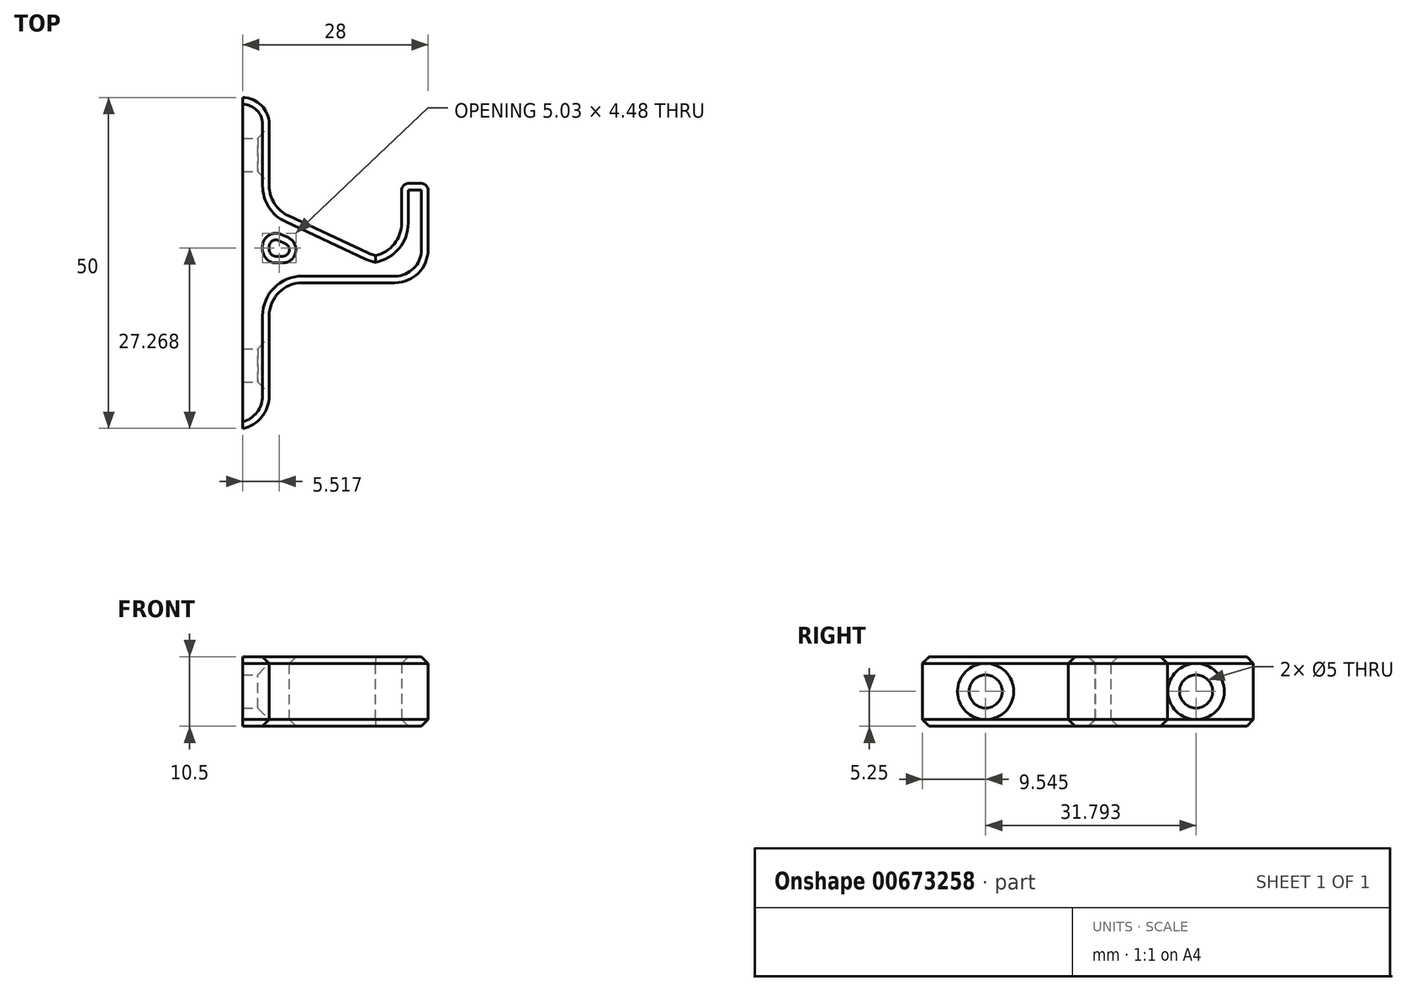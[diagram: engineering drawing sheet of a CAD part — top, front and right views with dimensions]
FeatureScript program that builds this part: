
annotation { "Feature Type Name" : "Feature", "Feature Type Description" : "" }
export const myFeature = defineFeature(function(context is Context, id is Id, definition is map)
    precondition{}
    {
        {
            var Q0;
            Q0=qCreatedBy(makeId("Top.planeOp"),FACE);
            var sketch = newSketch(context, id + "F0", { "sketchPlane" : qUnion([Q0])});
            skLineSegment(sketch, "E0", {"start": v(-37.83, 27.26) * mm, "end": v(-37.83, -22.74) * mm});
            skLineSegment(sketch, "E1", {"start": v(-37.83, -22.74) * mm, "end": v(-33.83, -22.74) * mm});
            skLineSegment(sketch, "E2", {"start": v(-33.83, -22.74) * mm, "end": v(-33.83, -0.71) * mm});
            skLineSegment(sketch, "E3", {"start": v(-33.83, -0.71) * mm, "end": v(-9.83, -0.71) * mm});
            skLineSegment(sketch, "E4", {"start": v(-9.83, -0.71) * mm, "end": v(-9.83, 14.29) * mm});
            skLineSegment(sketch, "E5", {"start": v(-9.83, 14.29) * mm, "end": v(-13.83, 14.29) * mm});
            skLineSegment(sketch, "E6", {"start": v(-13.83, 14.29) * mm, "end": v(-13.83, 3.29) * mm});
            skLineSegment(sketch, "E7", {"start": v(-13.83, 3.29) * mm, "end": v(-33.83, 3.29) * mm});
            skLineSegment(sketch, "E8", {"start": v(-33.83, 3.29) * mm, "end": v(-33.83, 27.26) * mm});
            skLineSegment(sketch, "E9", {"start": v(-33.83, 27.26) * mm, "end": v(-37.83, 27.26) * mm});
            skLineSegment(sketch, "E10", {"start": v(-33.83, 6.34) * mm, "end": v(-27.28, 3.29) * mm});
            skLineSegment(sketch, "E11", {"start": v(-27.28, 3.29) * mm, "end": v(-17.81, 3.29) * mm});
            skLineSegment(sketch, "E12", {"start": v(-17.81, 3.29) * mm, "end": v(-33.83, 10.76) * mm});
            skLineSegment(sketch, "E13", {"start": v(-33.83, -8.74) * mm, "end": v(741.82, -0.71) * mm});
            skLineSegment(sketch, "E14", {"start": v(-33.83, -4.74) * mm, "end": v(355.5, -0.71) * mm});
            skSolve(sketch);
        }
        {
            var Q0;
            Q0=makeQuery(id+"F0.imprint","IMPRINT",FACE,{"disambiguationData":[TD([[makeQuery(id+"F0.imprint","IMPRINT",EDGE,{"derivedFrom":sQuery(id+"F0.wireOp",EDGE,"E0")}),1.0]])]});
            var Q1;
            {var subQ0=sQuery(id+"F0.wireOp",EDGE,"E10");Q1=makeQuery(id+"F0.imprint","IMPRINT",FACE,{"disambiguationData":[TD([[makeQuery(id+"F0.imprint","IMPRINT",EDGE,{"derivedFrom":subQ0}),1.0]])]});}
            var Q2;
            {var subQ0=sQuery(id+"F0.wireOp",EDGE,"E13");Q2=makeQuery(id+"F0.imprint","IMPRINT",FACE,{"disambiguationData":[TD([[makeQuery(id+"F0.imprint","IMPRINT",EDGE,{"derivedFrom":subQ0}),1.0]])]});}
            extrude(context, id + "F1", {"entities" : qUnion([Q0, Q1, Q2]), "depth" : 10.5 * mm, "offsetDistance" : 25 * mm});
        }
        {
            var Q0;
            Q0=makeQuery(id+"F1.opExtrude","SWEPT_EDGE",EDGE,{"disambiguationData":[OSD([sQuery(id+"F0.wireOp",EDGE,"E6"),sQuery(id+"F0.wireOp",EDGE,"E7")])]});
            var Q1;
            Q1=makeQuery(id+"F1.opExtrude","SWEPT_EDGE",EDGE,{"disambiguationData":[OSD([sQuery(id+"F0.wireOp",EDGE,"E7"),sQuery(id+"F0.wireOp",EDGE,"E11"),sQuery(id+"F0.wireOp",EDGE,"E12")])]});
            var Q2;
            Q2=makeQuery(id+"F1.opExtrude","SWEPT_EDGE",EDGE,{"disambiguationData":[OSD([sQuery(id+"F0.wireOp",EDGE,"E3"),sQuery(id+"F0.wireOp",EDGE,"E14")])]});
            var Q3;
            Q3=makeQuery(id+"F1.opExtrude","SWEPT_EDGE",EDGE,{"disambiguationData":[OSD([sQuery(id+"F0.wireOp",EDGE,"E2"),sQuery(id+"F0.wireOp",EDGE,"E14")])]});
            var Q4;
            Q4=makeQuery(id+"F1.opExtrude","SWEPT_EDGE",EDGE,{"disambiguationData":[OSD([sQuery(id+"F0.wireOp",EDGE,"E8"),sQuery(id+"F0.wireOp",EDGE,"E12")])]});
            fillet(context, id + "F2", {"entities" : qUnion([Q0, Q1, Q2, Q3, Q4]), "radius" : 5 * mm, "tangentPropagation" : true, "allowEdgeOverflow" : false});
        }
        {
            var Q0;
            Q0=makeQuery(id+"F1.opExtrude","SWEPT_EDGE",EDGE,{"disambiguationData":[OSD([sQuery(id+"F0.wireOp",EDGE,"E4"),sQuery(id+"F0.wireOp",EDGE,"E5")])]});
            var Q1;
            Q1=makeQuery(id+"F1.opExtrude","SWEPT_EDGE",EDGE,{"disambiguationData":[OSD([sQuery(id+"F0.wireOp",EDGE,"E5"),sQuery(id+"F0.wireOp",EDGE,"E6")])]});
            var Q2;
            Q2=makeQuery(id+"F1.opExtrude","SWEPT_EDGE",EDGE,{"disambiguationData":[OSD([sQuery(id+"F0.wireOp",EDGE,"E8"),sQuery(id+"F0.wireOp",EDGE,"E10")])]});
            var Q3;
            Q3=makeQuery(id+"F1.opExtrude","SWEPT_EDGE",EDGE,{"disambiguationData":[OSD([sQuery(id+"F0.wireOp",EDGE,"E7"),sQuery(id+"F0.wireOp",EDGE,"E10"),sQuery(id+"F0.wireOp",EDGE,"E11")])]});
            var Q4;
            Q4=makeQuery(id+"F1.opExtrude","SWEPT_EDGE",EDGE,{"disambiguationData":[OSD([sQuery(id+"F0.wireOp",EDGE,"E7"),sQuery(id+"F0.wireOp",EDGE,"E8")])]});
            var Q5;
            Q5=makeQuery(id+"F1.opExtrude","SWEPT_EDGE",EDGE,{"disambiguationData":[OSD([sQuery(id+"F0.wireOp",EDGE,"E2"),sQuery(id+"F0.wireOp",EDGE,"E3")])]});
            var Q6;
            Q6=makeQuery(id+"F1.opExtrude","SWEPT_EDGE",EDGE,{"disambiguationData":[OSD([sQuery(id+"F0.wireOp",EDGE,"E2"),sQuery(id+"F0.wireOp",EDGE,"E13")])]});
            var Q7;
            Q7=makeQuery(id+"F1.opExtrude","SWEPT_EDGE",EDGE,{"disambiguationData":[OSD([sQuery(id+"F0.wireOp",EDGE,"E3"),sQuery(id+"F0.wireOp",EDGE,"E13")])]});
            fillet(context, id + "F3", {"entities" : qUnion([Q0, Q1, Q2, Q3, Q4, Q5, Q6, Q7]), "radius" : 1 * mm, "tangentPropagation" : true, "allowEdgeOverflow" : false});
        }
        {
            var Q0;
            Q0=makeQuery(id+"F1.opExtrude","SWEPT_EDGE",EDGE,{"disambiguationData":[OSD([sQuery(id+"F0.wireOp",EDGE,"E8"),sQuery(id+"F0.wireOp",EDGE,"E9")])]});
            var Q1;
            Q1=makeQuery(id+"F1.opExtrude","SWEPT_EDGE",EDGE,{"disambiguationData":[OSD([sQuery(id+"F0.wireOp",EDGE,"E1"),sQuery(id+"F0.wireOp",EDGE,"E2")])]});
            var Q2;
            Q2=makeQuery(id+"F1.opExtrude","SWEPT_EDGE",EDGE,{"disambiguationData":[OSD([sQuery(id+"F0.wireOp",EDGE,"E3"),sQuery(id+"F0.wireOp",EDGE,"E4")])]});
            fillet(context, id + "F4", {"entities" : qUnion([Q0, Q1, Q2]), "radius" : 4 * mm, "tangentPropagation" : true, "allowEdgeOverflow" : false});
        }
        {
            var Q0;
            {var subQ0=sQuery(id+"F0.wireOp",EDGE,"E7");Q0=makeQuery(id+"F1.opExtrude","CAP_EDGE",EDGE,{"disambiguationData":[OSD([subQ0]),TDD([makeQuery(id+"F0.imprint","IMPRINT",EDGE,{"disambiguationData":[TD([[makeQuery(id+"F0.imprint","INTERSECT",VERTEX,{"derivedFrom":[sQuery(id+"F0.wireOp",EDGE,"E6"),subQ0]}),-1.0]])],"derivedFrom":subQ0})])],"isStart":false});}
            var Q1;
            {var subQ0=sQuery(id+"F0.wireOp",EDGE,"E7");Q1=makeQuery(id+"F1.opExtrude","CAP_EDGE",EDGE,{"disambiguationData":[OSD([subQ0]),TDD([makeQuery(id+"F0.imprint","IMPRINT",EDGE,{"disambiguationData":[TD([[makeQuery(id+"F0.imprint","INTERSECT",VERTEX,{"derivedFrom":[sQuery(id+"F0.wireOp",EDGE,"E6"),subQ0]}),-1.0]])],"derivedFrom":subQ0})])],"isStart":true});}
            var Q2;
            Q2=makeQuery(id+"F1.opExtrude","CAP_EDGE",EDGE,{"disambiguationData":[OSD([sQuery(id+"F0.wireOp",EDGE,"E13")])],"isStart":true});
            var Q3;
            {var subQ0=sQuery(id+"F0.wireOp",EDGE,"E7");Q3=makeQuery(id+"F1.opExtrude","CAP_EDGE",EDGE,{"disambiguationData":[OSD([subQ0]),TDD([makeQuery(id+"F0.imprint","IMPRINT",EDGE,{"disambiguationData":[TD([[makeQuery(id+"F0.imprint","INTERSECT",VERTEX,{"derivedFrom":[subQ0,sQuery(id+"F0.wireOp",EDGE,"E8")]}),1.0]])],"derivedFrom":subQ0})])],"isStart":true});}
            var Q4;
            Q4=makeQuery(id+"F1.opExtrude","CAP_EDGE",EDGE,{"disambiguationData":[OSD([sQuery(id+"F0.wireOp",EDGE,"E10")])],"isStart":false});
            var Q5;
            Q5=makeQuery(id+"F1.opExtrude","CAP_EDGE",EDGE,{"disambiguationData":[OSD([sQuery(id+"F0.wireOp",EDGE,"E13")])],"isStart":false});
            var Q6;
            Q6=makeQuery(id+"F1.opExtrude","CAP_EDGE",EDGE,{"disambiguationData":[OSD([sQuery(id+"F0.wireOp",EDGE,"E3")])],"isStart":false});
            var Q7;
            Q7=makeQuery(id+"F1.opExtrude","CAP_EDGE",EDGE,{"disambiguationData":[OSD([sQuery(id+"F0.wireOp",EDGE,"E12")])],"isStart":false});
            var Q8;
            Q8=makeQuery(id+"F1.opExtrude","CAP_EDGE",EDGE,{"disambiguationData":[OSD([sQuery(id+"F0.wireOp",EDGE,"E3")])],"isStart":true});
            var Q9;
            Q9=makeQuery(id+"F1.opExtrude","CAP_EDGE",EDGE,{"disambiguationData":[OSD([sQuery(id+"F0.wireOp",EDGE,"E12")])],"isStart":true});
            chamfer(context, id + "F5", {"entities" : qUnion([Q0, Q1, Q2, Q3, Q4, Q5, Q6, Q7, Q8, Q9]), "width" : 1 * mm, "tangentPropagation" : true});
        }
        {
            var Q0;
            {var subQ0=sQuery(id+"F0.wireOp",EDGE,"E8");Q0=makeQuery(id+"F1.opExtrude","SWEPT_FACE",FACE,{"disambiguationData":[OSD([subQ0]),TDD([makeQuery(id+"F0.imprint","IMPRINT",EDGE,{"disambiguationData":[TD([[makeQuery(id+"F0.imprint","INTERSECT",VERTEX,{"derivedFrom":[subQ0,sQuery(id+"F0.wireOp",EDGE,"E9")]}),1.0]])],"derivedFrom":subQ0})])]});}
            var sketch = newSketch(context, id + "F6", { "sketchPlane" : qUnion([Q0])});
            skPoint(sketch, "E15", {"position": v(18.6, 5.25) * mm});
            skPoint(sketch, "E15.positionSnap0", {"position": v(18.6, 9.5) * mm});
            skPoint(sketch, "E15.positionSnap1", {"position": v(23.26, 5.25) * mm});
            skSolve(sketch);
        }
        {
            var Q0;
            {var subQ0=sQuery(id+"F0.wireOp",EDGE,"E2");Q0=makeQuery(id+"F1.opExtrude","SWEPT_FACE",FACE,{"disambiguationData":[OSD([subQ0]),TDD([makeQuery(id+"F0.imprint","IMPRINT",EDGE,{"disambiguationData":[TD([[makeQuery(id+"F0.imprint","INTERSECT",VERTEX,{"derivedFrom":[sQuery(id+"F0.wireOp",EDGE,"E1"),subQ0]}),-1.0]])],"derivedFrom":subQ0})])]});}
            var sketch = newSketch(context, id + "F7", { "sketchPlane" : qUnion([Q0])});
            skPoint(sketch, "E16", {"position": v(-13.2, 5.25) * mm});
            skPoint(sketch, "E16.positionSnap0", {"position": v(-13.2, 16.75) * mm});
            skPoint(sketch, "E16.positionSnap1", {"position": v(-17.85, 5.25) * mm});
            skSolve(sketch);
        }
        {
            var Q0;
            Q0=sQuery(id+"F6.wireOp",VERTEX,"E15");
            var Q1;
            Q1=sQuery(id+"F7.wireOp",VERTEX,"E16");
            var Q2;
            Q2=makeQuery(id+"F1.opExtrude","SWEPT_BODY",BODY,{"disambiguationData":[OSD([sQuery(id+"F0.wireOp",EDGE,"E0"),sQuery(id+"F0.wireOp",EDGE,"E1"),sQuery(id+"F0.wireOp",EDGE,"E2"),sQuery(id+"F0.wireOp",EDGE,"E3"),sQuery(id+"F0.wireOp",EDGE,"E4"),sQuery(id+"F0.wireOp",EDGE,"E5"),sQuery(id+"F0.wireOp",EDGE,"E6"),sQuery(id+"F0.wireOp",EDGE,"E7"),sQuery(id+"F0.wireOp",EDGE,"E8"),sQuery(id+"F0.wireOp",EDGE,"E9"),sQuery(id+"F0.wireOp",EDGE,"E10"),sQuery(id+"F0.wireOp",EDGE,"E12"),sQuery(id+"F0.wireOp",EDGE,"E13"),sQuery(id+"F0.wireOp",EDGE,"E14")])]});
            hole(context, id + "F8", {"style" : HoleStyle.C_SINK, "endStyle" : HoleEndStyle.BLIND, "holeDiameter" : 5 * mm, "cSinkDiameter" : 8.5 * mm, "cSinkAngle" : 90 * degree, "majorDiameter" : 5 * mm, "holeDepth" : 10 * mm, "isTappedThrough" : true, "tappedDepth" : 12 * mm, "tapClearance" : 3, "locations" : qUnion([Q0, Q1]), "scope" : qUnion([Q2])});
        }
    });
